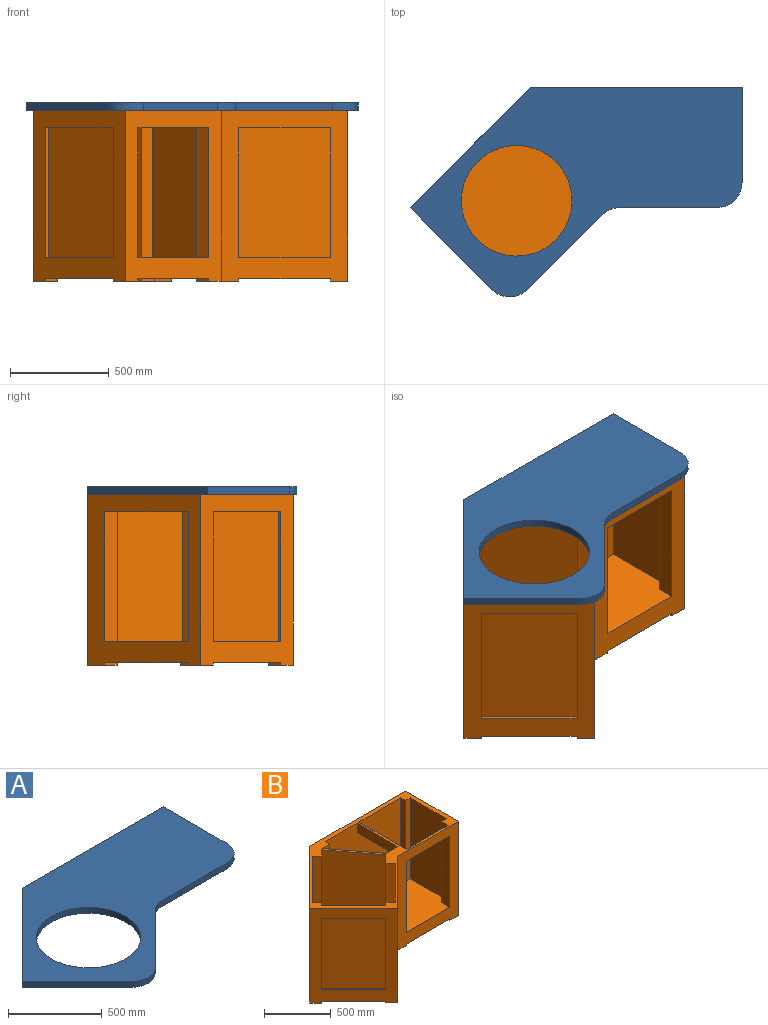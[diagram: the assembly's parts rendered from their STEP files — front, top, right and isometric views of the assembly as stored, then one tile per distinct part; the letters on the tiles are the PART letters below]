
ASSEMBLY  parts=2 mates=1
PART A: 12 faces, bbox 1677.5x1060.9x38.1 mm
  f0: cylinder r=127mm len=89.8mm, axis (0,0,1), area 3800.3mm2, adj f1,f9,f10,f11
  f1: plane 491.01x38.1mm, normal (0,-1,0), area 18707.3mm2, adj f0,f2,f10,f11
  f2: cylinder r=127mm len=127mm, axis (0,0,1), area 7600.6mm2, adj f1,f3,f10,f11
  f3: plane 482.6x38.1mm, normal (1,0,0), area 18387.1mm2, adj f2,f4,f10,f11
  f4: plane 1066.8x38.1mm, normal (0,1,0), area 40645.1mm2, adj f3,f5,f10,f11
  f5: plane 610.66x610.66mm, normal (-0.71,0.71,0), area 32903.2mm2, adj f4,f6,f10,f11
  f6: plane 413.09x413.09mm, normal (-0.71,-0.71,0), area 22258mm2, adj f5,f7,f10,f11
  f7: cylinder r=127mm len=179.61mm, axis (0,0,1), area 7600.6mm2, adj f6,f9,f10,f11
  f8: cylinder r=279.4mm len=558.8mm, axis (0,0,1), area 66885.4mm2, adj f10,f11
  f9: plane 376.95x376.95mm, normal (0.71,-0.71,0), area 20310.7mm2, adj f0,f7,f10,f11
  f10: plane 1677.46x1060.95mm, normal (0,0,-1), area 838271.6mm2, adj f0,f1,f2,f3,f4,f5,f6,f7
  f11: plane 1677.46x1060.95mm, normal (0,0,1), area 838271.6mm2, adj f0,f1,f2,f3,f4,f5,f6,f7
PART B: 94 faces, bbox 1590.7x1041.7x863.6 mm
  f0: plane 354.72x354.72mm, normal (0,0,1), area 9193.5mm2, adj f1,f2,f67,f92
  f1: plane 654.3x13.47mm, normal (0.71,-0.71,0), area 12464.5mm2, adj f0,f62,f67,f92
  f2: plane 654.3x13.47mm, normal (-0.71,0.71,0), area 12464.5mm2, adj f0,f62,f67,f92
  f3: plane 889.95x838.59mm, normal (0,0,1), area 434338.4mm2, adj f4,f5,f40,f43,f44,f45,f46,f52
  f4: plane 743.2x56.07mm, normal (0.71,-0.71,0), area 58931.7mm2, adj f3,f40,f55,f90
  f5: plane 743.2x77.29mm, normal (-0.71,0.71,0), area 81233.1mm2, adj f3,f55,f74,f90
  f6: plane 929.06x520.7mm, normal (0,0,1), area 380036.2mm2, adj f7,f39,f41,f49,f50,f53,f65,f73
  f7: plane 743.2x50.8mm, normal (0,-1,0), area 37754.8mm2, adj f6,f41,f55,f89
  f8: plane 654.3x19.05mm, normal (0,1,0), area 12464.5mm2, adj f11,f66,f69,f88
  f9: plane 654.3x19.05mm, normal (1,0,0), area 12464.5mm2, adj f12,f51,f82,f87
  f10: plane 654.3x19.05mm, normal (-1,0,0), area 12464.5mm2, adj f12,f51,f82,f87
  f11: plane 381x19.05mm, normal (0,0,1), area 7258mm2, adj f8,f42,f66,f88
  f12: plane 801.38x19.05mm, normal (0,0,-1), area 15266.2mm2, adj f9,f10,f51,f87
  f13: plane 101.35x88.9mm, normal (1,0,0), area 5632.2mm2, adj f24,f30,f51,f54,f78,f84
  f14: plane 101.35x62.86mm, normal (-0.71,-0.71,0), area 5632.2mm2, adj f23,f33,f52,f54,f80,f84
  f15: plane 101.35x88.9mm, normal (-1,0,0), area 5632.2mm2, adj f16,f29,f51,f70,f78,f85
  f16: plane 101.35x88.9mm, normal (0,-1,0), area 5632.2mm2, adj f15,f32,f66,f70,f79,f85
  f17: plane 101.35x62.86mm, normal (0.71,-0.71,0), area 5632.2mm2, adj f18,f38,f67,f71,f81,f83
  f18: plane 101.35x62.86mm, normal (0.71,0.71,0), area 5632.2mm2, adj f17,f37,f52,f71,f80,f83
  f19: plane 101.35x62.86mm, normal (-0.71,0.71,0), area 5632.2mm2, adj f20,f38,f67,f72,f81,f83
  f20: plane 101.35x62.86mm, normal (0.71,0.71,0), area 5632.2mm2, adj f19,f35,f68,f72,f80,f83
  f21: plane 101.35x88.9mm, normal (0,1,0), area 5632.2mm2, adj f22,f32,f66,f77,f79,f85
  f22: plane 101.35x88.9mm, normal (-1,0,0), area 5632.2mm2, adj f21,f28,f65,f77,f78,f85
  f23: plane 101.35x62.86mm, normal (0.71,-0.71,0), area 9009.7mm2, adj f14,f24,f54,f84
  f24: plane 101.35x88.9mm, normal (0,-1,0), area 9009.7mm2, adj f13,f23,f54,f84
  f25: plane 125.72x101.35mm, normal (0,1,0), area 12741.6mm2, adj f26,f31,f47,f76,f84
  f26: plane 101.35x88.9mm, normal (-0.71,0.71,0), area 12741.6mm2, adj f25,f34,f48,f76,f84
  f27: plane 482.6x88.65mm, normal (1,0,0), area 42780.6mm2, adj f28,f29,f78,f85
  f28: plane 424.95x88.65mm, normal (0,1,0), area 37670.4mm2, adj f22,f27,f78,f85
  f29: plane 424.95x88.65mm, normal (0,-1,0), area 37670.4mm2, adj f15,f27,f78,f85
  f30: plane 338.32x88.65mm, normal (0,-1,0), area 29991mm2, adj f13,f31,f78,f84
  f31: plane 431.8x88.65mm, normal (-1,0,0), area 38277.3mm2, adj f25,f30,f78,f84
  f32: plane 381x88.65mm, normal (-1,0,0), area 33774.1mm2, adj f16,f21,f79,f85
  f33: plane 88.65x65.79mm, normal (0.71,-0.71,0), area 8247.5mm2, adj f14,f34,f80,f84
  f34: plane 377.17x377.17mm, normal (0.71,0.71,0), area 47283.8mm2, adj f26,f33,f80,f84
  f35: plane 330.25x330.25mm, normal (-0.71,0.71,0), area 41401mm2, adj f20,f36,f80,f83
  f36: plane 413.09x413.09mm, normal (-0.71,-0.71,0), area 51787mm2, adj f35,f37,f80,f83
  f37: plane 330.25x330.25mm, normal (0.71,-0.71,0), area 41401mm2, adj f18,f36,f80,f83
  f38: plane 341.25x341.25mm, normal (0.71,0.71,0), area 42780.6mm2, adj f17,f19,f81,f83
  f39: plane 743.2x50.8mm, normal (1,0,0), area 37754.8mm2, adj f6,f53,f55,f86
  f40: plane 743.2x62.86mm, normal (-0.71,-0.71,0), area 64377.3mm2, adj f3,f4,f52,f55,f58,f63
  f41: plane 743.2x50.8mm, normal (-1,0,0), area 37754.8mm2, adj f6,f7,f55,f86
  f42: plane 654.3x19.05mm, normal (0,-1,0), area 12464.5mm2, adj f11,f66,f69,f88
  f43: plane 743.2x35.92mm, normal (0.71,-0.71,0), area 37754.8mm2, adj f3,f44,f55,f93
  f44: plane 743.2x62.86mm, normal (0.71,0.71,0), area 64377.3mm2, adj f3,f43,f52,f55,f58,f63
  f45: plane 743.2x35.92mm, normal (-0.71,0.71,0), area 37754.8mm2, adj f3,f46,f55,f93
  f46: plane 743.2x62.86mm, normal (0.71,0.71,0), area 64377.3mm2, adj f3,f45,f55,f60,f61,f68
  f47: plane 88.9x12.7mm, normal (1,0,0), area 1129mm2, adj f25,f65,f76,f78
  f48: plane 62.86x62.86mm, normal (-0.71,-0.71,0), area 1129mm2, adj f26,f68,f76,f80
  f49: plane 743.2x50.8mm, normal (0,1,0), area 37754.8mm2, adj f6,f50,f55,f89
  f50: plane 743.2x88.9mm, normal (-1,0,0), area 64377.3mm2, adj f6,f49,f55,f56,f57,f65
  f51: plane 1016x863.6mm, normal (0,1,0), area 342896.3mm2, adj f9,f10,f12,f13,f15,f52,f54,f55
  f52: plane 863.6x574.74mm, normal (-0.71,0.71,0), area 302948mm2, adj f3,f14,f18,f40,f44,f51,f54,f55
  f53: plane 743.2x76.88mm, normal (0,-1,0), area 57140.9mm2, adj f6,f39,f55,f91
  f54: plane 214.62x151.76mm, normal (0,0,-1), area 19080mm2, adj f13,f14,f23,f24,f51,f52
  f55: plane 1590.74x1041.71mm, normal (0,0,1), area 181838.5mm2, adj f4,f5,f7,f39,f40,f41,f43,f44
  f56: plane 520.7x463.05mm, normal (0,0,-1), area 18377.6mm2, adj f50,f57,f59,f64,f65,f73,f86
  f57: plane 444x88.9mm, normal (0,1,0), area 39471.9mm2, adj f50,f55,f56,f64
  f58: plane 436.45x436.45mm, normal (0,0,-1), area 11395.3mm2, adj f40,f44,f52,f63
  f59: plane 431.8x88.9mm, normal (-1,0,0), area 38387mm2, adj f55,f56,f75,f86
  f60: plane 357.19x357.19mm, normal (-0.71,0.71,0), area 44906.7mm2, adj f46,f55,f61,f74
  f61: plane 370.66x370.66mm, normal (0,0,-1), area 9622.9mm2, adj f46,f60,f68,f74
  f62: plane 354.72x354.72mm, normal (0,0,-1), area 9193.5mm2, adj f1,f2,f67,f92
  f63: plane 422.97x422.97mm, normal (0.71,-0.71,0), area 53177.9mm2, adj f40,f44,f55,f58
  f64: plane 501.65x88.9mm, normal (1,0,0), area 44596.7mm2, adj f55,f56,f57,f86
  f65: plane 863.6x640.85mm, normal (0,-1,0), area 244582.5mm2, adj f6,f22,f47,f50,f55,f56,f66,f68
  f66: plane 863.6x558.8mm, normal (1,0,0), area 228451.2mm2, adj f8,f11,f16,f21,f42,f51,f55,f65
  f67: plane 863.6x466.97mm, normal (-0.71,-0.71,0), area 248425.3mm2, adj f0,f1,f2,f17,f19,f52,f55,f62
  f68: plane 863.6x482.91mm, normal (0.71,-0.71,0), area 252856.1mm2, adj f3,f20,f46,f48,f55,f61,f65,f67
  f69: plane 381x19.05mm, normal (0,0,-1), area 7258.1mm2, adj f8,f42,f66,f88
  f70: plane 88.9x88.9mm, normal (0,0,-1), area 7903.2mm2, adj f15,f16,f51,f66
  f71: plane 125.72x125.72mm, normal (0,0,-1), area 7903.2mm2, adj f17,f18,f52,f67
  f72: plane 125.72x125.72mm, normal (0,0,-1), area 7903.2mm2, adj f19,f20,f67,f68
  f73: plane 654.3x88.9mm, normal (1,0,0), area 58167.6mm2, adj f6,f56,f65,f75
  f74: plane 743.2x62.86mm, normal (-0.71,-0.71,0), area 64377.3mm2, adj f3,f5,f55,f60,f61,f68
  f75: plane 743.2x122.23mm, normal (0,1,0), area 90845.2mm2, adj f6,f55,f59,f73,f91
  f76: plane 214.62x151.76mm, normal (0,0,-1), area 19080mm2, adj f25,f26,f47,f48,f65,f68
  f77: plane 88.9x88.9mm, normal (0,0,-1), area 7903.2mm2, adj f21,f22,f65,f66
  f78: plane 801.38x558.8mm, normal (0,0,-1), area 66561.8mm2, adj f13,f15,f22,f27,f28,f29,f30,f31
  f79: plane 381x38.1mm, normal (0,0,-1), area 14516.1mm2, adj f16,f21,f32,f66
  f80: plane 889.95x824.16mm, normal (0,0,-1), area 64294.3mm2, adj f14,f18,f20,f33,f34,f35,f36,f37
  f81: plane 368.19x368.19mm, normal (0,0,-1), area 18387.1mm2, adj f17,f19,f38,f67
  f82: plane 801.38x19.05mm, normal (0,0,1), area 15266.2mm2, adj f9,f10,f51,f87
  f83: plane 743.34x743.34mm, normal (0,0,-1), area 297359.4mm2, adj f17,f18,f19,f20,f35,f36,f37,f38
  f84: plane 591.79x520.7mm, normal (0,0,-1), area 201488.5mm2, adj f13,f14,f23,f24,f25,f26,f30,f31
  f85: plane 482.6x475.75mm, normal (0,0,-1), area 224437.3mm2, adj f15,f16,f21,f22,f27,f28,f29,f32
  f86: plane 801.38x743.2mm, normal (0,-1,0), area 593892.6mm2, adj f6,f39,f41,f55,f56,f59,f64
  f87: plane 801.38x654.3mm, normal (0,1,0), area 524343.8mm2, adj f9,f10,f12,f82
  f88: plane 654.3x381mm, normal (1,0,0), area 249289.8mm2, adj f8,f11,f42,f69
  f89: plane 743.2x381mm, normal (-1,0,0), area 283160.7mm2, adj f6,f7,f49,f55
  f90: plane 743.2x385.82mm, normal (-0.79,-0.61,0), area 361716.5mm2, adj f3,f4,f5,f55
  f91: plane 743.2x381mm, normal (0.79,0.61,0), area 357197.7mm2, adj f6,f53,f55,f75
  f92: plane 654.3x341.25mm, normal (-0.71,-0.71,0), area 315767.1mm2, adj f0,f1,f2,f62
  f93: plane 743.2x341.25mm, normal (0.71,0.71,0), area 358670.3mm2, adj f3,f43,f45,f55
PLACE A rot(axis=(0,0,-1),0deg) t=(0,0,38.1)mm
PLACE B at identity
MATE fastened A.f4 <-> B.f51  axis (0,1,0) through (0,0,0)mm
